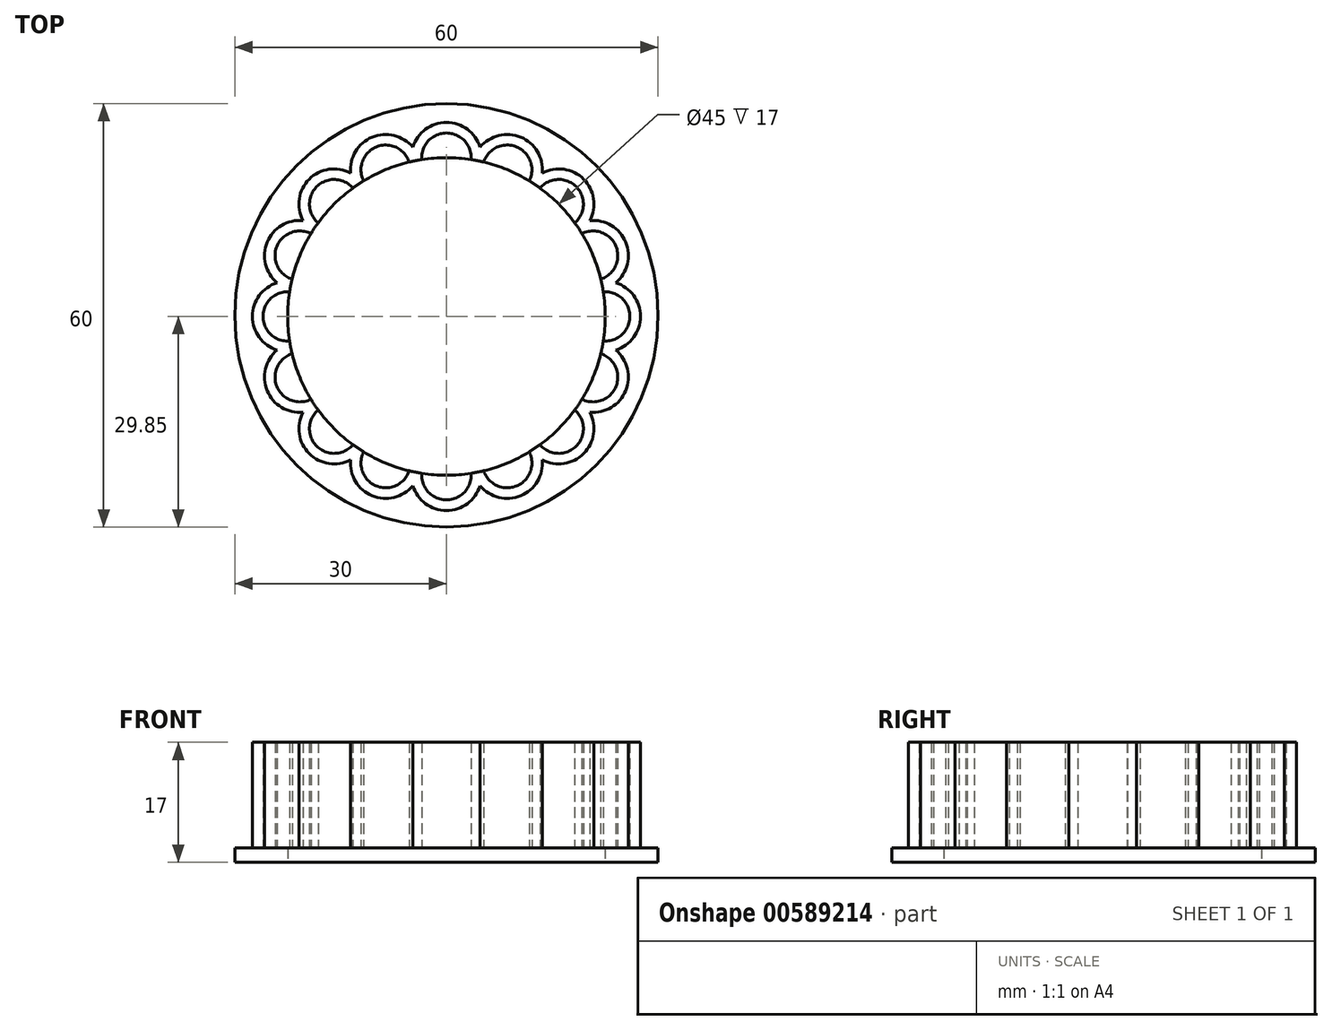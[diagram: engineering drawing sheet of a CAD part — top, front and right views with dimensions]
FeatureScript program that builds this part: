
annotation { "Feature Type Name" : "Feature", "Feature Type Description" : "" }
export const myFeature = defineFeature(function(context is Context, id is Id, definition is map)
    precondition{}
    {
        {
            var Q0;
            Q0=qCreatedBy(makeId("Top.planeOp"),FACE);
            var sketch = newSketch(context, id + "F0", { "sketchPlane" : qUnion([Q0])});
            skCircle(sketch, "E0", {"center": v(0, 0.15) * mm, "radius": 30 * mm});
            skCircle(sketch, "E1", {"center": v(0, 0) * mm, "radius": 22.5 * mm});
            skSolve(sketch);
        }
        {
            var Q0;
            Q0 = qSketchRegion(id + "F0", true);
            extrude(context, id + "F1", {"entities" : qUnion([Q0]), "depth" : 2 * mm, "offsetDistance" : 25 * mm});
        }
        {
            var Q0;
            Q0=makeQuery(id+"F1.opExtrude","CAP_FACE",FACE,{"disambiguationData":[OSD([sQuery(id+"F0.wireOp",EDGE,"E0"),sQuery(id+"F0.wireOp",EDGE,"E1")])],"isStart":false});
            var sketch = newSketch(context, id + "F2", { "sketchPlane" : qUnion([Q0])});
            skArc(sketch, "E2", {"start": v(-3.49, 22.23) * mm, "mid": v(-4.23, 22.1) * mm, "end": v(-4.97, 21.94) * mm});
            skArc(sketch, "E3", {"start": v(4.97, 21.94) * mm, "mid": v(0, 27.5) * mm, "end": v(-4.97, 21.94) * mm});
            skArc(sketch, "E4.0", {"start": v(3.49, 22.23) * mm, "mid": v(0, 26) * mm, "end": v(-3.49, 22.23) * mm});
            skArc(sketch, "E5.trimOffspring", {"start": v(4.97, 21.94) * mm, "mid": v(4.23, 22.1) * mm, "end": v(3.49, 22.23) * mm});
            skArc(sketch, "E6.1.0", {"start": v(-3.8, 22.18) * mm, "mid": v(-10.52, 25.4) * mm, "end": v(-12.99, 18.37) * mm});
            skArc(sketch, "E6.1.1", {"start": v(-5.28, 21.87) * mm, "mid": v(-9.95, 24.02) * mm, "end": v(-11.73, 19.2) * mm});
            skArc(sketch, "E6.2.0", {"start": v(-12, 19.03) * mm, "mid": v(-19.45, 19.45) * mm, "end": v(-19.03, 12) * mm});
            skArc(sketch, "E6.2.1", {"start": v(-13.25, 18.18) * mm, "mid": v(-18.38, 18.38) * mm, "end": v(-18.18, 13.25) * mm});
            skArc(sketch, "E6.3.0", {"start": v(-18.37, 12.99) * mm, "mid": v(-25.4, 10.52) * mm, "end": v(-22.18, 3.8) * mm});
            skArc(sketch, "E6.3.1", {"start": v(-19.2, 11.73) * mm, "mid": v(-24.02, 9.95) * mm, "end": v(-21.87, 5.28) * mm});
            skArc(sketch, "E6.4.0", {"start": v(-21.94, 4.97) * mm, "mid": v(-27.5, 0) * mm, "end": v(-21.94, -4.97) * mm});
            skArc(sketch, "E6.4.1", {"start": v(-22.23, 3.49) * mm, "mid": v(-26, 0) * mm, "end": v(-22.23, -3.49) * mm});
            skArc(sketch, "E6.5.0", {"start": v(-22.18, -3.8) * mm, "mid": v(-25.4, -10.52) * mm, "end": v(-18.37, -12.99) * mm});
            skArc(sketch, "E6.5.1", {"start": v(-21.87, -5.28) * mm, "mid": v(-24.02, -9.95) * mm, "end": v(-19.2, -11.73) * mm});
            skArc(sketch, "E6.6.0", {"start": v(-19.03, -12) * mm, "mid": v(-19.45, -19.45) * mm, "end": v(-12, -19.03) * mm});
            skArc(sketch, "E6.6.1", {"start": v(-18.18, -13.25) * mm, "mid": v(-18.38, -18.38) * mm, "end": v(-13.25, -18.18) * mm});
            skArc(sketch, "E6.7.0", {"start": v(-12.99, -18.37) * mm, "mid": v(-10.52, -25.4) * mm, "end": v(-3.8, -22.18) * mm});
            skArc(sketch, "E6.7.1", {"start": v(-11.73, -19.2) * mm, "mid": v(-9.95, -24.02) * mm, "end": v(-5.28, -21.87) * mm});
            skArc(sketch, "E6.8.0", {"start": v(-4.97, -21.94) * mm, "mid": v(0, -27.5) * mm, "end": v(4.97, -21.94) * mm});
            skArc(sketch, "E6.8.1", {"start": v(-3.49, -22.23) * mm, "mid": v(0, -26) * mm, "end": v(3.49, -22.23) * mm});
            skArc(sketch, "E6.9.0", {"start": v(3.8, -22.18) * mm, "mid": v(10.52, -25.4) * mm, "end": v(12.99, -18.37) * mm});
            skArc(sketch, "E6.9.1", {"start": v(5.28, -21.87) * mm, "mid": v(9.95, -24.02) * mm, "end": v(11.73, -19.2) * mm});
            skArc(sketch, "E6.10.0", {"start": v(12, -19.03) * mm, "mid": v(19.45, -19.45) * mm, "end": v(19.03, -12) * mm});
            skArc(sketch, "E6.10.1", {"start": v(13.25, -18.18) * mm, "mid": v(18.38, -18.38) * mm, "end": v(18.18, -13.25) * mm});
            skArc(sketch, "E6.11.0", {"start": v(18.37, -12.99) * mm, "mid": v(25.4, -10.52) * mm, "end": v(22.18, -3.8) * mm});
            skArc(sketch, "E6.11.1", {"start": v(19.2, -11.73) * mm, "mid": v(24.02, -9.95) * mm, "end": v(21.87, -5.28) * mm});
            skCircle(sketch, "E7", {"center": v(0, 0) * mm, "radius": 22.5 * mm});
            skArc(sketch, "E8.3.12.0", {"start": v(21.94, -4.97) * mm, "mid": v(27.5, 0) * mm, "end": v(21.94, 4.97) * mm});
            skArc(sketch, "E8.4.12.0", {"start": v(22.23, -3.49) * mm, "mid": v(26, 0) * mm, "end": v(22.23, 3.49) * mm});
            skArc(sketch, "E9.3.13.0", {"start": v(22.18, 3.8) * mm, "mid": v(25.4, 10.52) * mm, "end": v(18.37, 12.99) * mm});
            skArc(sketch, "E9.4.13.0", {"start": v(21.87, 5.28) * mm, "mid": v(24.02, 9.95) * mm, "end": v(19.2, 11.73) * mm});
            skArc(sketch, "E10.3.14.0", {"start": v(19.03, 12) * mm, "mid": v(19.45, 19.45) * mm, "end": v(12, 19.03) * mm});
            skArc(sketch, "E10.4.14.0", {"start": v(18.18, 13.25) * mm, "mid": v(18.38, 18.38) * mm, "end": v(13.25, 18.18) * mm});
            skArc(sketch, "E10.3.15.0", {"start": v(12.99, 18.37) * mm, "mid": v(10.52, 25.4) * mm, "end": v(3.8, 22.18) * mm});
            skArc(sketch, "E10.4.15.0", {"start": v(11.73, 19.2) * mm, "mid": v(9.95, 24.02) * mm, "end": v(5.28, 21.87) * mm});
            skSolve(sketch);
        }
        {
            var Q0;
            Q0 = qSketchRegion(id + "F2", true);
            extrude(context, id + "F3", {"entities" : qUnion([Q0]), "operationType" : NewBodyOperationType.ADD, "depth" : 15 * mm, "offsetDistance" : 25 * mm});
        }
    });
